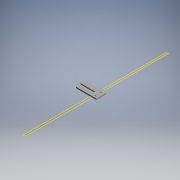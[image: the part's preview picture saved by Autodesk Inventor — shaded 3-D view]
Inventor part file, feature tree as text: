
AUTODESK INVENTOR PART (.ipt)
format: ipt  version: 2018 (Build 220112000, 112)  size: 120,832 bytes
history: native  units: mm
features: other x6, reference x2, plane x1, extrude x1, fillet x1, sketch x1
ambient origin geometry x8: Origin, YZ Plane, XZ Plane, XY Plane, X Axis, Y Axis, Z Axis, Center Point
bodies: Solid1 (feature_tree)
feature tree (12):
  plane  "Work Plane1"
  extrude  "Extrusion1"  Depth=15.0mm
  fillet  "Fillet1"  Radius=5.0mm
  sketch  "Sketch1"  dims[d0=5.0mm d1=15.0mm d4=5.0mm d5=5.0mm d6=6.0mm d7=0.0mm d8=15.0mm]
  reference  "Reference1"
  reference  "Reference2"
  other  "Main assembly Test.iam"
  other  "Assembly33:1"
  other  "Top-Front-BRace:1"
  other  "3030 600mm_CPY3:1"
  other  "Assembly31:1"
  other  "3030 600mm:2"
